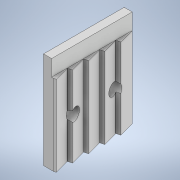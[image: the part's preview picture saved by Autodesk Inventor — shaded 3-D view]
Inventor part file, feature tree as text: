
AUTODESK INVENTOR PART (.ipt)
format: ipt  version: 2022 (Build 260153000, 153)  size: 154,112 bytes
history: native  units: mm
features: sketch x2, extrude x2, other x1, hole x1
ambient origin geometry x8: Origin, YZ Plane, XZ Plane, XY Plane, X Axis, Y Axis, Z Axis, Center Point
bodies: Body1 (feature_tree)
feature tree (6):
  other  "Sólido1"
  sketch  "Esboço1"  dims[d3=24.0mm d4=0.0mm d5=20.0mm d6=0.0mm]
  extrude  "Extrusão1"  Depth=20.0mm TaperAngle=0.0deg
  extrude  "Extrusão2"  [1 undecoded]
  hole  "Furo1"  [1 undecoded]
  sketch  "Esboço2"  dims[d7=3.0mm d8=6.0mm d9=4.0mm d10=2.0mm d11=90.0deg d12=8.0mm d13=20.594885mm]
note: 2 required parameter values undecoded (feature->parameter linkage not recoverable at this tier; creation-order binding heuristic only, values carry confidence <= 0.55)
